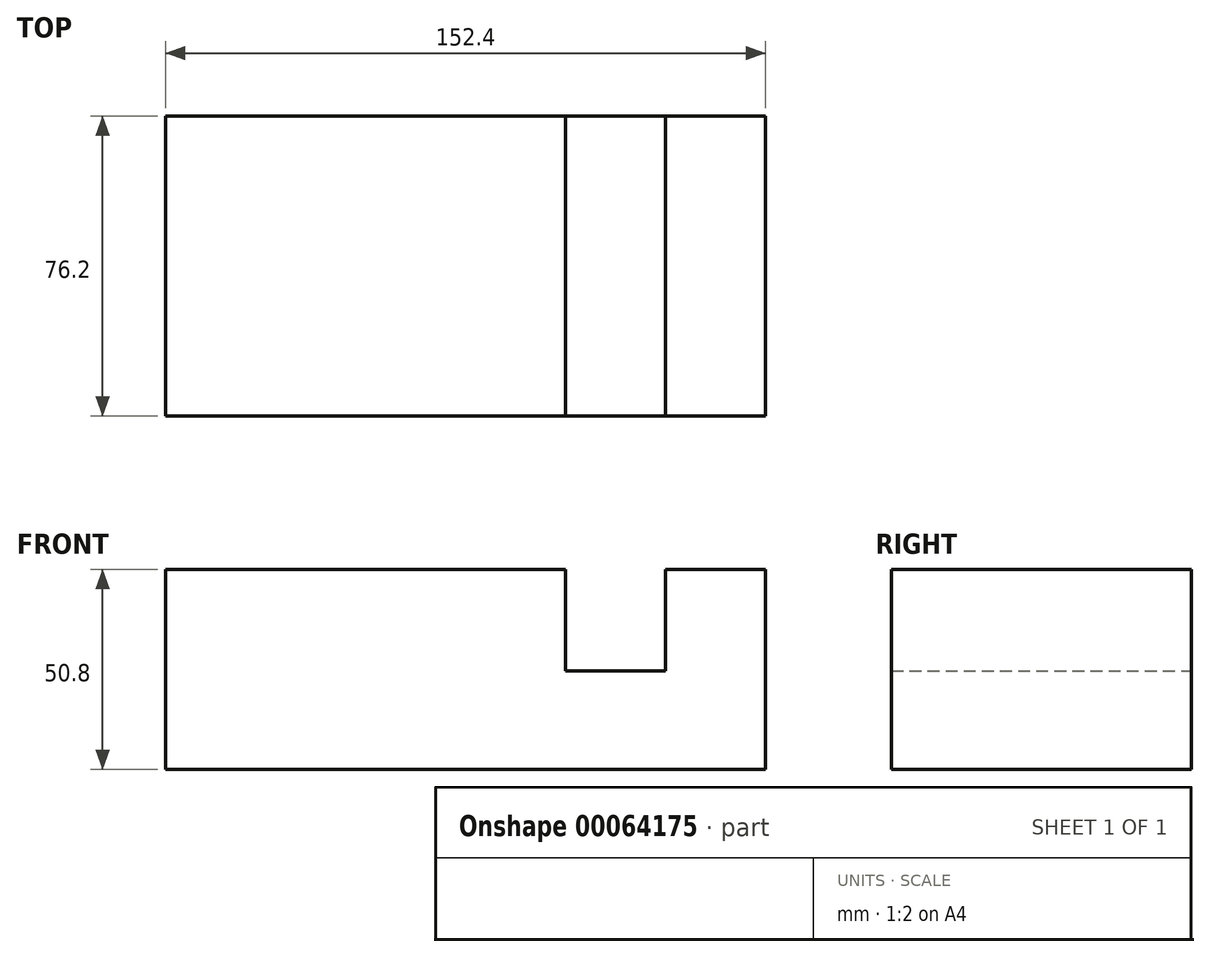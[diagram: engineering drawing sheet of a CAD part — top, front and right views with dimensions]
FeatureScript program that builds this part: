
annotation { "Feature Type Name" : "Feature", "Feature Type Description" : "" }
export const myFeature = defineFeature(function(context is Context, id is Id, definition is map)
    precondition{}
    {
        {
            var Q0;
            Q0=qCreatedBy(makeId("Front.planeOp"),FACE);
            var sketch = newSketch(context, id + "F0", { "sketchPlane" : qUnion([Q0])});
            skLineSegment(sketch, "E0", {"start": v(-75.27, -25.01) * mm, "end": v(77.13, -25.01) * mm});
            skLineSegment(sketch, "E1", {"start": v(77.13, -25.01) * mm, "end": v(77.13, 25.79) * mm});
            skLineSegment(sketch, "E2", {"start": v(77.13, 25.79) * mm, "end": v(51.73, 25.79) * mm});
            skLineSegment(sketch, "E3", {"start": v(51.73, 25.79) * mm, "end": v(51.73, 0) * mm});
            skLineSegment(sketch, "E4", {"start": v(51.73, 0) * mm, "end": v(26.33, 0) * mm});
            skLineSegment(sketch, "E5", {"start": v(26.33, 0) * mm, "end": v(26.33, 25.79) * mm});
            skLineSegment(sketch, "E6", {"start": v(26.33, 25.79) * mm, "end": v(-75.27, 25.79) * mm});
            skLineSegment(sketch, "E7", {"start": v(-75.27, 25.79) * mm, "end": v(-75.27, -25.01) * mm});
            skSolve(sketch);
        }
        {
            var Q0;
            Q0 = qSketchRegion(id + "F0", true);
            extrude(context, id + "F1", {"entities" : qUnion([Q0]), "depth" : 76.2 * mm});
        }
    });
